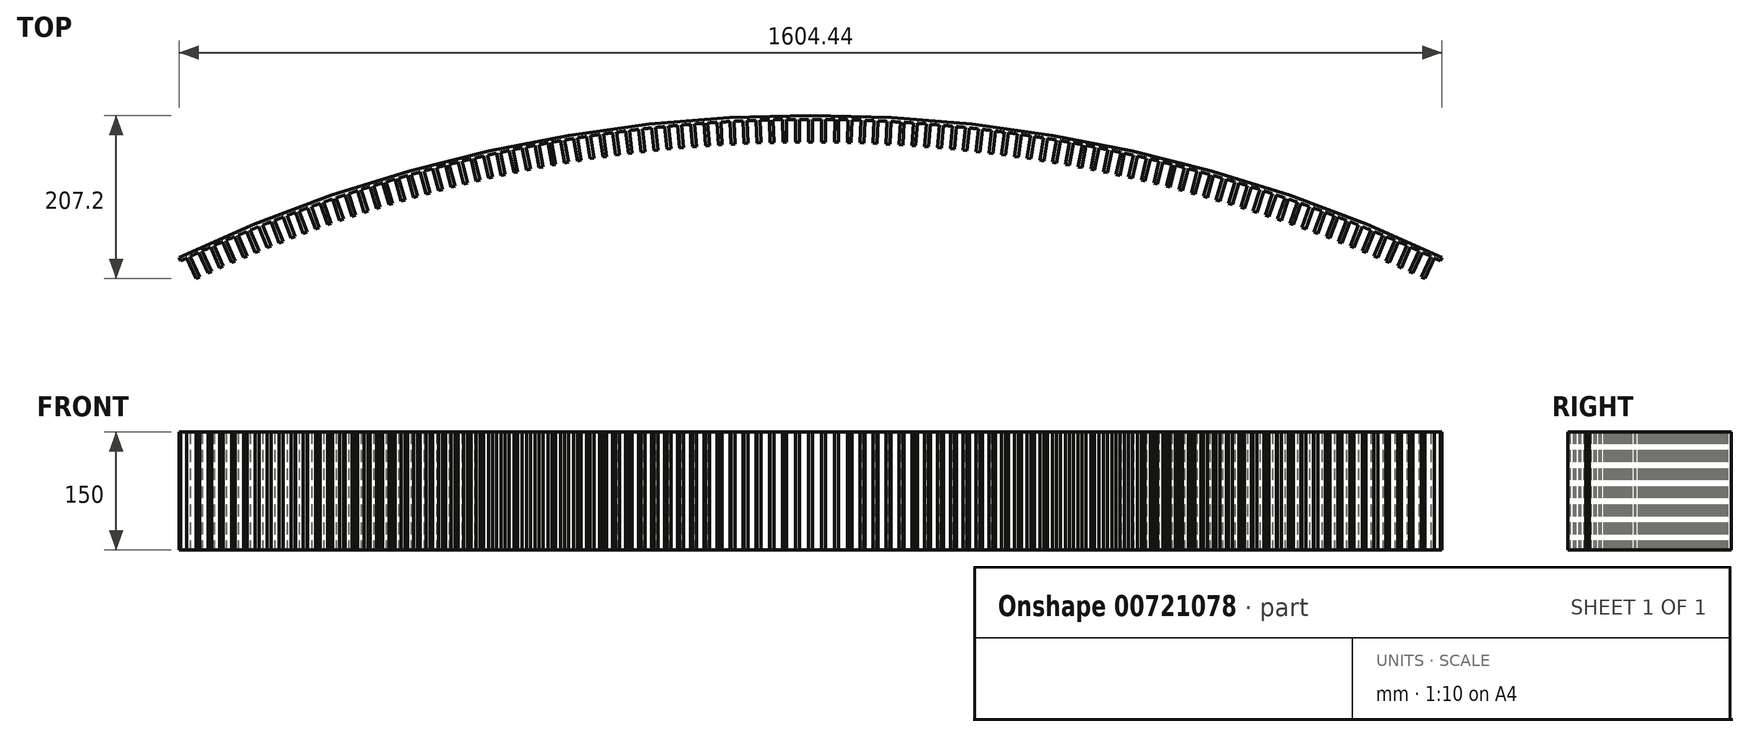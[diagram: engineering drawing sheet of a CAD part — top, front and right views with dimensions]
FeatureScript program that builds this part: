
annotation { "Feature Type Name" : "Feature", "Feature Type Description" : "" }
export const myFeature = defineFeature(function(context is Context, id is Id, definition is map)
    precondition{}
    {
        {
            var Q0;
            Q0=qCreatedBy(makeId("Top.planeOp"),FACE);
            var sketch = newSketch(context, id + "F0", { "sketchPlane" : qUnion([Q0])});
            skArc(sketch, "E0", {"start": v(900, -32.13) * mm, "mid": v(0, 194.55) * mm, "end": v(-900, -32.13) * mm, "construction": true});
            skArc(sketch, "E1.0", {"start": v(802.22, -11.18) * mm, "mid": v(0, 169.15) * mm, "end": v(-802.22, -11.18) * mm});
            skCircle(sketch, "E2", {"center": v(-900, -32.13) * mm, "radius": 100 * mm, "construction": true});
            skCircle(sketch, "E3", {"center": v(900, -32.13) * mm, "radius": 100 * mm, "construction": true});
            skArc(sketch, "E4.0", {"start": v(800.08, -15.7) * mm, "mid": v(0, 164.15) * mm, "end": v(-800.08, -15.7) * mm});
            skLineSegment(sketch, "E5", {"start": v(-800.08, -15.7) * mm, "end": v(-802.22, -11.18) * mm});
            skLineSegment(sketch, "E6", {"start": v(802.22, -11.18) * mm, "end": v(800.08, -15.7) * mm});
            skSolve(sketch);
        }
        {
            var Q0;
            Q0 = qSketchRegion(id + "F0", true);
            extrude(context, id + "F1", {"entities" : qUnion([Q0]), "endBound" : BoundingType.SYMMETRIC, "depth" : 150 * mm, "offsetDistance" : 25 * mm});
        }
        {
            var Q0;
            Q0=qCreatedBy(makeId("Top.planeOp"),FACE);
            var sketch = newSketch(context, id + "F2", { "sketchPlane" : qUnion([Q0])});
            skArc(sketch, "E7.0", {"start": v(800.08, -15.7) * mm, "mid": v(0, 164.15) * mm, "end": v(-800.08, -15.7) * mm});
            skLineSegment(sketch, "E8", {"start": v(0, 165.49) * mm, "end": v(0, 135.49) * mm, "construction": true});
            skLineSegment(sketch, "E9.bottom", {"start": v(2.5, 135.49) * mm, "end": v(-2.5, 135.49) * mm});
            skLineSegment(sketch, "E9.left", {"start": v(2.5, 135.49) * mm, "end": v(2.5, 165.49) * mm});
            skLineSegment(sketch, "E9.right", {"start": v(-2.5, 135.49) * mm, "end": v(-2.5, 165.49) * mm});
            skPoint(sketch, "E9.middle", {"position": v(0, 150.49) * mm});
            skLineSegment(sketch, "E10", {"start": v(-2.5, 165.49) * mm, "end": v(2.5, 165.49) * mm});
            skSolve(sketch);
        }
        {
            var Q0;
            Q0 = qSketchRegion(id + "F2", true);
            extrude(context, id + "F3", {"entities" : qUnion([Q0]), "endBound" : BoundingType.SYMMETRIC, "depth" : 150 * mm, "offsetDistance" : 25 * mm});
        }
        {
            var Q0;
            Q0=qCreatedBy(makeId("Right.planeOp"),FACE);
            var sketch = newSketch(context, id + "F4", { "sketchPlane" : qUnion([Q0])});
            skPoint(sketch, "E11.0", {"position": v(-1705.45, 0) * mm});
            skLineSegment(sketch, "E12", {"start": v(-1705.45, 0) * mm, "end": v(-1705.45, 1038.35) * mm});
            skSolve(sketch);
        }
        {
            var Q0;
            Q0=makeQuery(id+"F3.opExtrude","SWEPT_BODY",BODY,{"disambiguationData":[OSD([sQuery(id+"F2.wireOp",EDGE,"E9.bottom"),sQuery(id+"F2.wireOp",EDGE,"E9.left"),sQuery(id+"F2.wireOp",EDGE,"E9.right"),sQuery(id+"F2.wireOp",EDGE,"E10")])]});
            var Q1;
            Q1=sQuery(id+"F4.wireOp",EDGE,"E12");
            circularPattern(context, id + "F5", {"operationType" : NewBodyOperationType.ADD, "entities" : qUnion([Q0]), "axis" : qUnion([Q1]), "angle" : 25 * degree, "instanceCount" : 50, "equalSpace" : true, "isCentered" : true});
        }
    });
